# Revit family: BuzziSpace - BuzziShade - Square2
name_source: partatom
category: Lighting Fixtures
units: mm (PartAtom-declared; Revit-internal decimal feet)

## family parameters
Always vertical = Yes
Cut with Voids When Loaded = No
Host = Ceiling
Light Source = Yes
OmniClass Number = 23.80.70.11
OmniClass Title = Luminaries for Internal Lighting
Part Type = Normal
Room Calculation Point = No
Round Connector Dimension = Use Diameter
Shared = No

## types (6) — shared parameters
Color Filter = 16777215
Description = BuzziShade Square
Dimming Lamp Color Temperature Shift = <None>
Light Source Symbol Size = 1' - 6"
Manufacturer = BuzziSpace
Model = BuzziShade
URL = https://www.buzzi.space

## per-type parameters (varying)
| type | Beam | Light Toggle | Medium |
| Retrofit Medium | No | 1 | Yes |
| Globe Medium | No | 2 | Yes |
| Spot Medium | No | 3 | Yes |
| Retrofit Beam | Yes | 1 | No |
| Spot Beam | Yes | 3 | No |
| Globe Beam | Yes | 2 | No |

## geometry (parser evidence)
native form markers: Sweep x13
no freeform markers — native parametric forms only
